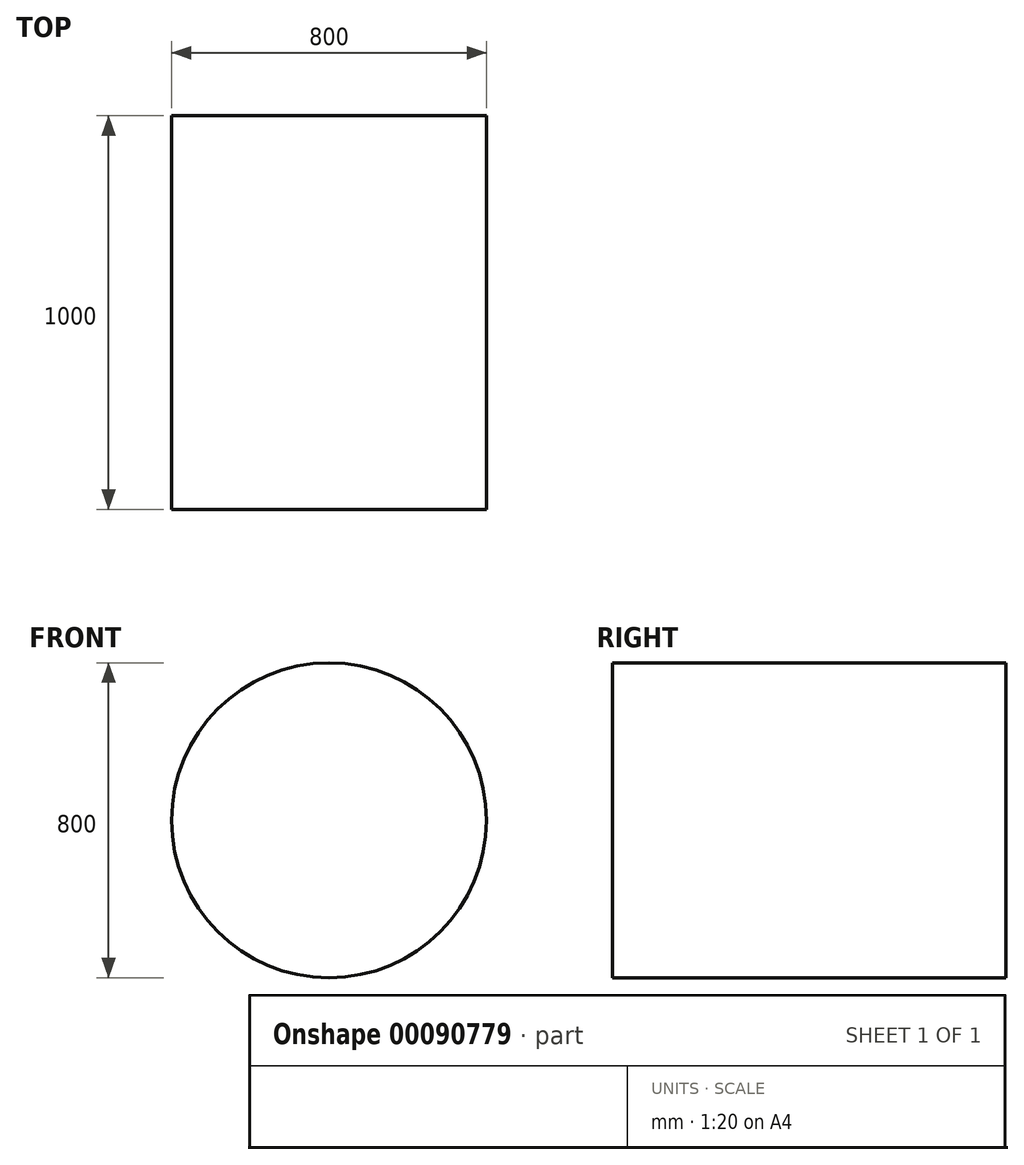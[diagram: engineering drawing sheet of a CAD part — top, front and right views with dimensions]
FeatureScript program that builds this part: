
annotation { "Feature Type Name" : "Feature", "Feature Type Description" : "" }
export const myFeature = defineFeature(function(context is Context, id is Id, definition is map)
    precondition{}
    {
        {
            var Q0;
            Q0=qCreatedBy(makeId("Front.planeOp"),FACE);
            var sketch = newSketch(context, id + "F0", { "sketchPlane" : qUnion([Q0])});
            skCircle(sketch, "E0", {"center": v(0, 0) * mm, "radius": 400 * mm});
            skSolve(sketch);
        }
        {
            var Q0;
            Q0 = qSketchRegion(id + "F0", true);
            var Q1;
            Q1=sQuery(id+"F0.wireOp",EDGE,"E0");
            extrude(context, id + "F1", {"entities" : qUnion([Q0]), "bodyType" : ToolBodyType.SURFACE, "surfaceEntities" : qUnion([Q1]), "depth" : 1000 * mm});
        }
    });
